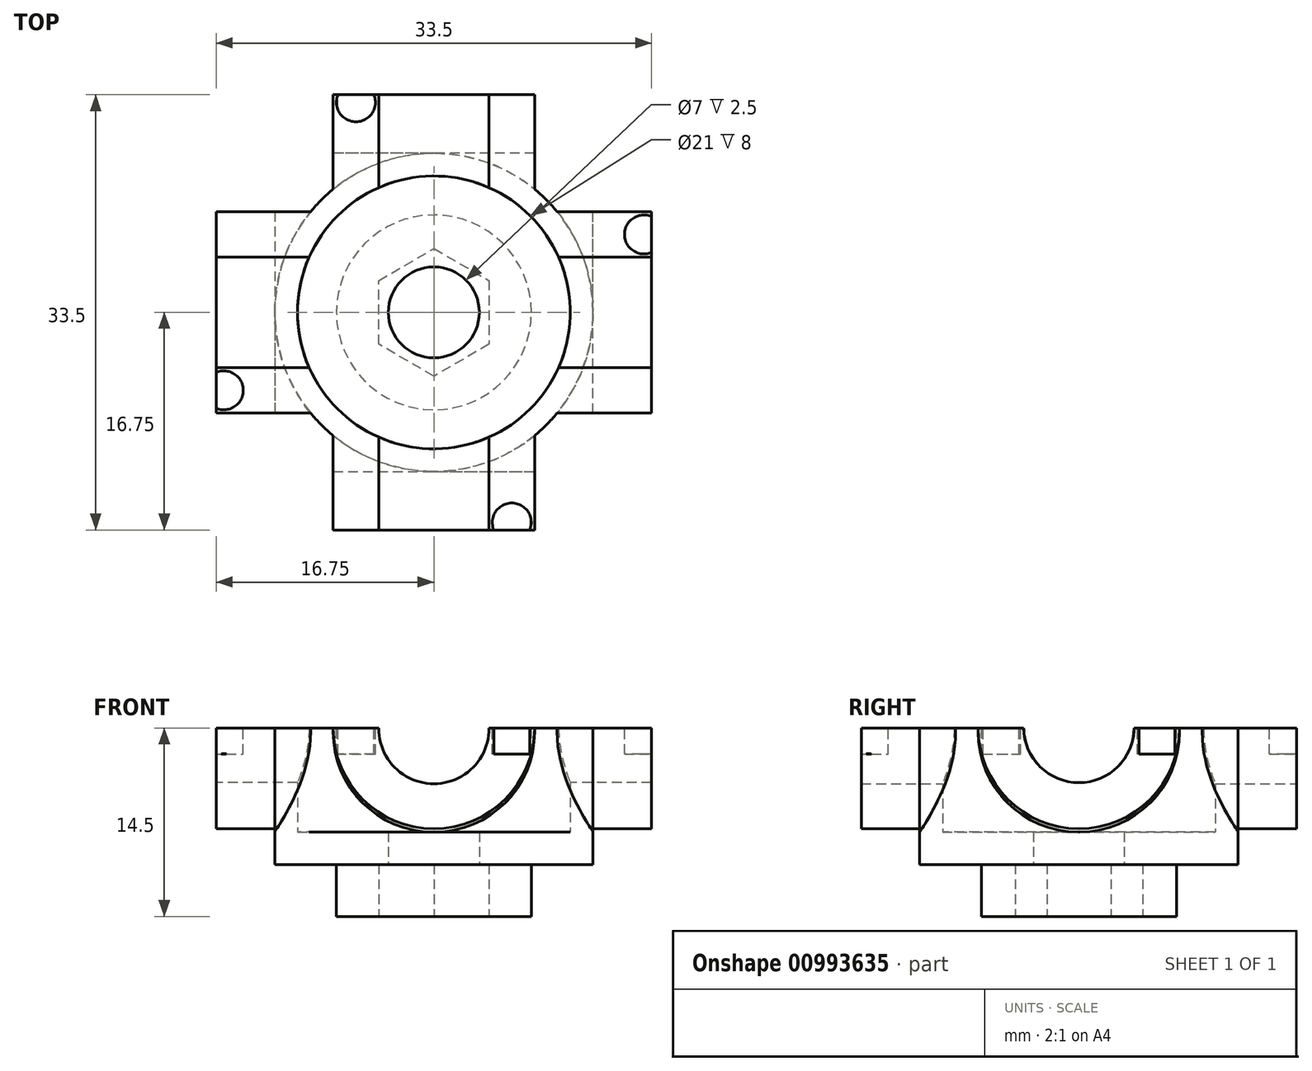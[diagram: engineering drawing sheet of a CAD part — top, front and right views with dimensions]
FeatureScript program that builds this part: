
annotation { "Feature Type Name" : "Feature", "Feature Type Description" : "" }
export const myFeature = defineFeature(function(context is Context, id is Id, definition is map)
    precondition{}
    {
        {
            var Q0;
            Q0=qCreatedBy(makeId("Top.planeOp"),FACE);
            var sketch = newSketch(context, id + "F0", { "sketchPlane" : qUnion([Q0])});
            skCircle(sketch, "E0.cCircle", {"center": v(0, 0) * mm, "radius": 4.25 * mm, "construction": true});
            skLineSegment(sketch, "E0.0", {"start": v(4.25, 2.45) * mm, "end": v(4.25, -2.45) * mm});
            skLineSegment(sketch, "E0.1", {"start": v(4.25, -2.45) * mm, "end": v(0, -4.9) * mm});
            skLineSegment(sketch, "E0.2", {"start": v(0, -4.9) * mm, "end": v(-4.25, -2.45) * mm});
            skLineSegment(sketch, "E0.3", {"start": v(-4.25, -2.45) * mm, "end": v(-4.25, 2.45) * mm});
            skLineSegment(sketch, "E0.4", {"start": v(-4.25, 2.45) * mm, "end": v(0, 4.9) * mm});
            skLineSegment(sketch, "E0.5", {"start": v(0, 4.9) * mm, "end": v(4.25, 2.45) * mm});
            skPoint(sketch, "E0.0.midPoint", {"position": v(4.25, 0) * mm});
            skCircle(sketch, "E1", {"center": v(0, 0) * mm, "radius": 3.5 * mm});
            skCircle(sketch, "E2", {"center": v(0, 0) * mm, "radius": 7.5 * mm});
            skSolve(sketch);
        }
        {
            var Q0;
            Q0=makeQuery(id+"F0.imprint","IMPRINT",FACE,{"disambiguationData":[TD([[makeQuery(id+"F0.imprint","IMPRINT",EDGE,{"derivedFrom":sQuery(id+"F0.wireOp",EDGE,"E0.0")}),1.0]])]});
            extrude(context, id + "F1", {"entities" : qUnion([Q0]), "depth" : 4 * mm, "offsetDistance" : 25 * mm});
        }
        {
            var Q0;
            Q0=makeQuery(id+"F1.opExtrude","CAP_FACE",FACE,{"disambiguationData":[OSD([sQuery(id+"F0.wireOp",EDGE,"E0.0"),sQuery(id+"F0.wireOp",EDGE,"E0.1"),sQuery(id+"F0.wireOp",EDGE,"E0.2"),sQuery(id+"F0.wireOp",EDGE,"E0.3"),sQuery(id+"F0.wireOp",EDGE,"E0.4"),sQuery(id+"F0.wireOp",EDGE,"E0.5"),sQuery(id+"F0.wireOp",EDGE,"E2")])],"isStart":false});
            var sketch = newSketch(context, id + "F2", { "sketchPlane" : qUnion([Q0])});
            skCircle(sketch, "E3", {"center": v(0, 0) * mm, "radius": 3.5 * mm});
            skCircle(sketch, "E4", {"center": v(0, 0) * mm, "radius": 12.25 * mm});
            skSolve(sketch);
        }
        {
            var Q0;
            Q0=makeQuery(id+"F2.imprint","IMPRINT",FACE,{"disambiguationData":[TD([[makeQuery(id+"F2.imprint","IMPRINT",EDGE,{"derivedFrom":sQuery(id+"F2.wireOp",EDGE,"E4")}),1.0]])]});
            var Q1;
            Q1=makeQuery(id+"F2.imprint","IMPRINT",FACE,{"disambiguationData":[TD([[makeQuery(id+"F2.imprint","IMPRINT",EDGE,{"derivedFrom":makeQuery(id+"F1.opExtrude","CAP_EDGE",EDGE,{"disambiguationData":[OSD([sQuery(id+"F0.wireOp",EDGE,"E0.0")])],"isStart":false})}),1.0]])]});
            var Q2;
            Q2=makeQuery(id+"F2.imprint","IMPRINT",FACE,{"disambiguationData":[TD([[makeQuery(id+"F2.imprint","IMPRINT",EDGE,{"derivedFrom":sQuery(id+"F2.wireOp",EDGE,"E3")}),-1.0]])]});
            extrude(context, id + "F3", {"entities" : qUnion([Q0, Q1, Q2]), "operationType" : NewBodyOperationType.ADD, "depth" : 2.5 * mm, "offsetDistance" : 25 * mm});
        }
        {
            var Q0;
            Q0=makeQuery(id+"F3.opExtrude","CAP_FACE",FACE,{"disambiguationData":[OSD([sQuery(id+"F2.wireOp",EDGE,"E3"),sQuery(id+"F2.wireOp",EDGE,"E4")])],"isStart":false});
            var sketch = newSketch(context, id + "F4", { "sketchPlane" : qUnion([Q0])});
            skLineSegment(sketch, "E5", {"start": v(0, 0) * mm, "end": v(-16.88, 16.88) * mm, "construction": true});
            skLineSegment(sketch, "E6", {"start": v(0, 0) * mm, "end": v(-26.34, 0) * mm, "construction": true});
            skCircle(sketch, "E7", {"center": v(0, 0) * mm, "radius": 16.75 * mm, "construction": true});
            skLineSegment(sketch, "E8", {"start": v(16.75, 0) * mm, "end": v(16.75, 7.75) * mm});
            skLineSegment(sketch, "E9", {"start": v(16.75, 7.75) * mm, "end": v(9.49, 7.75) * mm});
            skLineSegment(sketch, "E10", {"start": v(16.75, 0) * mm, "end": v(16.75, -7.75) * mm});
            skLineSegment(sketch, "E11", {"start": v(16.75, -7.75) * mm, "end": v(9.49, -7.75) * mm});
            skLineSegment(sketch, "E12.MirrorCS", {"start": v(-16.75, 7.75) * mm, "end": v(-9.49, 7.75) * mm});
            skLineSegment(sketch, "E13.MirrorCS", {"start": v(-16.75, 0) * mm, "end": v(-16.75, 7.75) * mm});
            skLineSegment(sketch, "E14.MirrorCS", {"start": v(-16.75, 0) * mm, "end": v(-16.75, -7.75) * mm});
            skLineSegment(sketch, "E15.MirrorCS", {"start": v(-16.75, -7.75) * mm, "end": v(-9.49, -7.75) * mm});
            skLineSegment(sketch, "E16.MirrorCS", {"start": v(-7.75, 16.75) * mm, "end": v(-7.75, 9.49) * mm});
            skLineSegment(sketch, "E17.MirrorCS", {"start": v(0, 16.75) * mm, "end": v(-7.75, 16.75) * mm});
            skLineSegment(sketch, "E18.MirrorCS", {"start": v(0, 16.75) * mm, "end": v(7.75, 16.75) * mm});
            skLineSegment(sketch, "E19.MirrorCS", {"start": v(7.75, 16.75) * mm, "end": v(7.75, 9.49) * mm});
            skLineSegment(sketch, "E20.MirrorCS", {"start": v(-7.75, -16.75) * mm, "end": v(-7.75, -9.49) * mm});
            skLineSegment(sketch, "E21.MirrorCS", {"start": v(0, -16.75) * mm, "end": v(-7.75, -16.75) * mm});
            skLineSegment(sketch, "E22.MirrorCS", {"start": v(0, -16.75) * mm, "end": v(7.75, -16.75) * mm});
            skLineSegment(sketch, "E23.MirrorCS", {"start": v(7.75, -16.75) * mm, "end": v(7.75, -9.49) * mm});
            skCircle(sketch, "E24", {"center": v(0, 0) * mm, "radius": 10.5 * mm});
            skSolve(sketch);
        }
        {
            var Q0;
            Q0=makeQuery(id+"F4.imprint","IMPRINT",FACE,{"disambiguationData":[TD([[makeQuery(id+"F4.imprint","IMPRINT",EDGE,{"derivedFrom":sQuery(id+"F4.wireOp",EDGE,"E24")}),-1.0]])]});
            var Q1;
            {var subQ1=sQuery(id+"F4.wireOp",EDGE,"E16.MirrorCS");Q1=makeQuery(id+"F4.imprint","IMPRINT",FACE,{"disambiguationData":[TD([[makeQuery(id+"F4.imprint","IMPRINT",EDGE,{"derivedFrom":subQ1}),1.0]])]});}
            var Q2;
            {var subQ1=sQuery(id+"F4.wireOp",EDGE,"E12.MirrorCS");Q2=makeQuery(id+"F4.imprint","IMPRINT",FACE,{"disambiguationData":[TD([[makeQuery(id+"F4.imprint","IMPRINT",EDGE,{"derivedFrom":subQ1}),-1.0]])]});}
            var Q3;
            Q3=makeQuery(id+"F4.imprint","IMPRINT",FACE,{"disambiguationData":[TD([[makeQuery(id+"F4.imprint","IMPRINT",EDGE,{"derivedFrom":sQuery(id+"F4.wireOp",EDGE,"E8")}),1.0]])]});
            var Q4;
            {var subQ1=sQuery(id+"F4.wireOp",EDGE,"E20.MirrorCS");Q4=makeQuery(id+"F4.imprint","IMPRINT",FACE,{"disambiguationData":[TD([[makeQuery(id+"F4.imprint","IMPRINT",EDGE,{"derivedFrom":subQ1}),-1.0]])]});}
            extrude(context, id + "F5", {"entities" : qUnion([Q0, Q1, Q2, Q3, Q4]), "operationType" : NewBodyOperationType.ADD, "depth" : 8 * mm, "offsetDistance" : 25 * mm});
        }
        {
            var Q0;
            Q0=makeQuery(id+"F5.opExtrude","SWEPT_FACE",FACE,{"disambiguationData":[OSD([sQuery(id+"F4.wireOp",EDGE,"E13.MirrorCS"),sQuery(id+"F4.wireOp",EDGE,"E14.MirrorCS")])]});
            var sketch = newSketch(context, id + "F6", { "sketchPlane" : qUnion([Q0])});
            skCircle(sketch, "E25", {"center": v(0, 14.5) * mm, "radius": 4.25 * mm, "construction": true});
            skArc(sketch, "E26", {"start": v(-4.25, 14.5) * mm, "mid": v(0, 10.3) * mm, "end": v(4.25, 14.5) * mm});
            skArc(sketch, "E27", {"start": v(-7.75, 14.5) * mm, "mid": v(0, 6.75) * mm, "end": v(7.75, 14.5) * mm});
            skSolve(sketch);
        }
        {
            var Q0;
            {var subQ0=sQuery(id+"F6.wireOp",EDGE,"E26");Q0=makeQuery(id+"F6.imprint","IMPRINT",FACE,{"disambiguationData":[TD([[makeQuery(id+"F6.imprint","IMPRINT",EDGE,{"derivedFrom":subQ0}),1.0]])]});}
            extrude(context, id + "F7", {"entities" : qUnion([Q0]), "operationType" : NewBodyOperationType.REMOVE, "endBound" : BoundingType.THROUGH_ALL, "oppositeDirection" : true, "depth" : 25 * mm, "offsetDistance" : 25 * mm});
        }
        {
            var Q0;
            Q0=makeQuery(id+"F6.imprint","IMPRINT",FACE,{"disambiguationData":[TD([[makeQuery(id+"F6.imprint","IMPRINT",EDGE,{"derivedFrom":sQuery(id+"F6.wireOp",EDGE,"E27")}),-1.0]])]});
            extrude(context, id + "F8", {"entities" : qUnion([Q0]), "operationType" : NewBodyOperationType.REMOVE, "oppositeDirection" : true, "depth" : 4.5 * mm, "offsetDistance" : 25 * mm});
        }
        {
            var Q0;
            Q0=makeQuery(id+"F5.opExtrude","SWEPT_FACE",FACE,{"disambiguationData":[OSD([sQuery(id+"F4.wireOp",EDGE,"E8"),sQuery(id+"F4.wireOp",EDGE,"E10")])]});
            var sketch = newSketch(context, id + "F9", { "sketchPlane" : qUnion([Q0])});
            skArc(sketch, "E28", {"start": v(-7.75, 14.5) * mm, "mid": v(0, 6.75) * mm, "end": v(7.75, 14.5) * mm});
            skSolve(sketch);
        }
        {
            var Q0;
            Q0=makeQuery(id+"F9.imprint","IMPRINT",FACE,{"disambiguationData":[TD([[makeQuery(id+"F9.imprint","IMPRINT",EDGE,{"derivedFrom":sQuery(id+"F9.wireOp",EDGE,"E28")}),-1.0]])]});
            extrude(context, id + "F10", {"entities" : qUnion([Q0]), "operationType" : NewBodyOperationType.REMOVE, "oppositeDirection" : true, "depth" : 4.5 * mm, "offsetDistance" : 25 * mm});
        }
        {
            var Q0;
            Q0=makeQuery(id+"F5.opExtrude","SWEPT_FACE",FACE,{"disambiguationData":[OSD([sQuery(id+"F4.wireOp",EDGE,"E17.MirrorCS"),sQuery(id+"F4.wireOp",EDGE,"E18.MirrorCS")])]});
            var sketch = newSketch(context, id + "F11", { "sketchPlane" : qUnion([Q0])});
            skCircle(sketch, "E29", {"center": v(0, 14.5) * mm, "radius": 4.25 * mm, "construction": true});
            skArc(sketch, "E30", {"start": v(-7.75, 14.5) * mm, "mid": v(0, 6.75) * mm, "end": v(7.75, 14.5) * mm});
            skArc(sketch, "E31", {"start": v(-4.25, 14.5) * mm, "mid": v(0, 10.21) * mm, "end": v(4.25, 14.5) * mm});
            skSolve(sketch);
        }
        {
            var Q0;
            {var subQ0=sQuery(id+"F11.wireOp",EDGE,"E31");Q0=makeQuery(id+"F11.imprint","IMPRINT",FACE,{"disambiguationData":[TD([[makeQuery(id+"F11.imprint","IMPRINT",EDGE,{"derivedFrom":subQ0}),1.0]])]});}
            extrude(context, id + "F12", {"entities" : qUnion([Q0]), "operationType" : NewBodyOperationType.REMOVE, "endBound" : BoundingType.THROUGH_ALL, "oppositeDirection" : true, "depth" : 25 * mm, "offsetDistance" : 25 * mm});
        }
        {
            var Q0;
            Q0=makeQuery(id+"F11.imprint","IMPRINT",FACE,{"disambiguationData":[TD([[makeQuery(id+"F11.imprint","IMPRINT",EDGE,{"derivedFrom":sQuery(id+"F11.wireOp",EDGE,"E30")}),-1.0]])]});
            extrude(context, id + "F13", {"entities" : qUnion([Q0]), "operationType" : NewBodyOperationType.REMOVE, "oppositeDirection" : true, "depth" : 4.5 * mm, "offsetDistance" : 25 * mm});
        }
        {
            var Q0;
            Q0=makeQuery(id+"F5.opExtrude","SWEPT_FACE",FACE,{"disambiguationData":[OSD([sQuery(id+"F4.wireOp",EDGE,"E21.MirrorCS"),sQuery(id+"F4.wireOp",EDGE,"E22.MirrorCS")])]});
            var sketch = newSketch(context, id + "F14", { "sketchPlane" : qUnion([Q0])});
            skArc(sketch, "E32", {"start": v(-7.75, 14.5) * mm, "mid": v(0, 6.75) * mm, "end": v(7.75, 14.5) * mm});
            skSolve(sketch);
        }
        {
            var Q0;
            Q0=makeQuery(id+"F14.imprint","IMPRINT",FACE,{"disambiguationData":[TD([[makeQuery(id+"F14.imprint","IMPRINT",EDGE,{"derivedFrom":sQuery(id+"F14.wireOp",EDGE,"E32")}),-1.0]])]});
            extrude(context, id + "F15", {"entities" : qUnion([Q0]), "operationType" : NewBodyOperationType.REMOVE, "oppositeDirection" : true, "depth" : 4.5 * mm, "offsetDistance" : 25 * mm});
        }
        {
            var Q0;
            Q0=makeQuery(id+"F5.opExtrude","CAP_EDGE",EDGE,{"disambiguationData":[OSD([sQuery(id+"F4.wireOp",EDGE,"E15.MirrorCS")])],"isStart":true});
            var Q1;
            Q1=makeQuery(id+"F5.opExtrude","CAP_EDGE",EDGE,{"disambiguationData":[OSD([sQuery(id+"F4.wireOp",EDGE,"E12.MirrorCS")])],"isStart":true});
            var Q2;
            Q2=makeQuery(id+"F5.opExtrude","CAP_EDGE",EDGE,{"disambiguationData":[OSD([sQuery(id+"F4.wireOp",EDGE,"E20.MirrorCS")])],"isStart":true});
            var Q3;
            Q3=makeQuery(id+"F5.opExtrude","CAP_EDGE",EDGE,{"disambiguationData":[OSD([sQuery(id+"F4.wireOp",EDGE,"E23.MirrorCS")])],"isStart":true});
            var Q4;
            Q4=makeQuery(id+"F5.opExtrude","CAP_EDGE",EDGE,{"disambiguationData":[OSD([sQuery(id+"F4.wireOp",EDGE,"E11")])],"isStart":true});
            var Q5;
            Q5=makeQuery(id+"F5.opExtrude","CAP_EDGE",EDGE,{"disambiguationData":[OSD([sQuery(id+"F4.wireOp",EDGE,"E9")])],"isStart":true});
            var Q6;
            Q6=makeQuery(id+"F5.opExtrude","CAP_EDGE",EDGE,{"disambiguationData":[OSD([sQuery(id+"F4.wireOp",EDGE,"E19.MirrorCS")])],"isStart":true});
            var Q7;
            Q7=makeQuery(id+"F5.opExtrude","CAP_EDGE",EDGE,{"disambiguationData":[OSD([sQuery(id+"F4.wireOp",EDGE,"E16.MirrorCS")])],"isStart":true});
            fillet(context, id + "F16", {"entities" : qUnion([Q0, Q1, Q2, Q3, Q4, Q5, Q6, Q7]), "radius" : 7.7 * mm, "tangentPropagation" : true, "allowEdgeOverflow" : false});
        }
        {
            var Q0;
            {var subQ0=sQuery(id+"F4.wireOp",EDGE,"E15.MirrorCS");var subQ1=sQuery(id+"F2.wireOp",EDGE,"E4");var subQ3=sQuery(id+"F4.wireOp",EDGE,"E20.MirrorCS");var subQ6=sQuery(id+"F4.wireOp",EDGE,"E14.MirrorCS");var subQ7=sQuery(id+"F4.wireOp",EDGE,"E13.MirrorCS");var subQ8=sQuery(id+"F4.wireOp",EDGE,"E12.MirrorCS");var subQ9=sQuery(id+"F4.wireOp",EDGE,"E9");var subQ10=sQuery(id+"F4.wireOp",EDGE,"E19.MirrorCS");var subQ12=sQuery(id+"F4.wireOp",EDGE,"E24");var subQ14=sQuery(id+"F4.wireOp",EDGE,"E18.MirrorCS");var subQ15=sQuery(id+"F4.wireOp",EDGE,"E17.MirrorCS");var subQ18=sQuery(id+"F4.wireOp",EDGE,"E11");var subQ19=sQuery(id+"F4.wireOp",EDGE,"E23.MirrorCS");var subQ21=makeQuery(id+"F5.opExtrude","SWEPT_FACE",FACE,{"disambiguationData":[OSD([subQ8])]});var subQ22=sQuery(id+"F4.wireOp",EDGE,"E16.MirrorCS");var subQ26=sQuery(id+"F4.wireOp",EDGE,"E10");var subQ27=sQuery(id+"F4.wireOp",EDGE,"E8");var subQ28=makeQuery(id+"F5.opExtrude","CAP_FACE",FACE,{"disambiguationData":[OSD([subQ1,subQ27,subQ9,subQ26,subQ18,subQ8,subQ7,subQ6,subQ0,subQ22,subQ15,subQ14,subQ10,subQ3,sQuery(id+"F4.wireOp",EDGE,"E21.MirrorCS"),sQuery(id+"F4.wireOp",EDGE,"E22.MirrorCS"),subQ19,subQ12])],"isStart":false});Q0=makeQuery(id+"F12.boolean.opBoolean","SPLIT",FACE,{"disambiguationData":[TD([subQ21])],"derivedFrom":makeQuery(id+"F7.boolean.opBoolean","SPLIT",FACE,{"disambiguationData":[TD([makeQuery(id+"F5.opExtrude","SWEPT_FACE",FACE,{"disambiguationData":[OSD([subQ9])]})])],"derivedFrom":subQ28})});}
            var sketch = newSketch(context, id + "F17", { "sketchPlane" : qUnion([Q0])});
            skLineSegment(sketch, "E33", {"start": v(0, 0) * mm, "end": v(16.6, 16.6) * mm, "construction": true});
            skLineSegment(sketch, "E34", {"start": v(0, 0) * mm, "end": v(22.28, 0) * mm, "construction": true});
            skCircle(sketch, "E35", {"center": v(0, 0) * mm, "radius": 17.25 * mm, "construction": true});
            skCircle(sketch, "E36", {"center": v(0, 0) * mm, "radius": 6 * mm, "construction": true});
            skLineSegment(sketch, "E37", {"start": v(-6, 0) * mm, "end": v(-6, 19.71) * mm, "construction": true});
            skLineSegment(sketch, "E38", {"start": v(6, 0) * mm, "end": v(6, 19.18) * mm, "construction": true});
            skLineSegment(sketch, "E39", {"start": v(0, 6) * mm, "end": v(19.02, 6) * mm, "construction": true});
            skLineSegment(sketch, "E40", {"start": v(0, -6) * mm, "end": v(19.02, -6) * mm, "construction": true});
            skCircle(sketch, "E41", {"center": v(-6, 16.17) * mm, "radius": 1.5 * mm});
            skCircle(sketch, "E42.MirrorC", {"center": v(6, 16.17) * mm, "radius": 1.5 * mm});
            skCircle(sketch, "E43.MirrorC", {"center": v(6, -16.17) * mm, "radius": 1.5 * mm});
            skCircle(sketch, "E44.MirrorC", {"center": v(-6, -16.17) * mm, "radius": 1.5 * mm});
            skCircle(sketch, "E45.MirrorC", {"center": v(16.17, 6) * mm, "radius": 1.5 * mm});
            skCircle(sketch, "E46.MirrorC", {"center": v(16.17, -6) * mm, "radius": 1.5 * mm});
            skCircle(sketch, "E47.MirrorC", {"center": v(-16.17, 6) * mm, "radius": 1.5 * mm});
            skCircle(sketch, "E48.MirrorC", {"center": v(-16.17, -6) * mm, "radius": 1.5 * mm});
            skSolve(sketch);
        }
        {
            var Q0;
            {var subQ0=sQuery(id+"F17.wireOp",EDGE,"E41");var subQ1=sQuery(id+"F4.wireOp",EDGE,"E18.MirrorCS");var subQ2=sQuery(id+"F4.wireOp",EDGE,"E17.MirrorCS");var subQ3=sQuery(id+"F4.wireOp",EDGE,"E16.MirrorCS");var subQ4=makeQuery(id+"F12.boolean.opBoolean","SPLIT",EDGE,{"disambiguationData":[TD([makeQuery(id+"F5.opExtrude","SWEPT_FACE",FACE,{"disambiguationData":[OSD([subQ3])]})])],"derivedFrom":makeQuery(id+"F5.opExtrude","CAP_EDGE",EDGE,{"disambiguationData":[OSD([subQ2,subQ1])],"isStart":false})});var subQ5=makeQuery(id+"F17.imprint","INTERSECT",VERTEX,{"disambiguationData":[OD(0.0)],"derivedFrom":[subQ4,subQ0]});Q0=makeQuery(id+"F17.imprint","IMPRINT",FACE,{"disambiguationData":[TD([[makeQuery(id+"F17.imprint","IMPRINT",EDGE,{"disambiguationData":[TD([[subQ5,1.0]])],"derivedFrom":subQ0}),1.0]])]});}
            var Q1;
            Q1=makeQuery(id+"F17.imprint","IMPRINT",FACE,{"disambiguationData":[TD([[makeQuery(id+"F17.imprint","IMPRINT",EDGE,{"derivedFrom":sQuery(id+"F17.wireOp",EDGE,"E42.MirrorC")}),-1.0]])]});
            var Q2;
            Q2=makeQuery(id+"F17.imprint","IMPRINT",FACE,{"disambiguationData":[TD([[makeQuery(id+"F17.imprint","IMPRINT",EDGE,{"derivedFrom":sQuery(id+"F17.wireOp",EDGE,"E46.MirrorC")}),-1.0]])]});
            var Q3;
            Q3=makeQuery(id+"F17.imprint","IMPRINT",FACE,{"disambiguationData":[TD([[makeQuery(id+"F17.imprint","IMPRINT",EDGE,{"derivedFrom":sQuery(id+"F17.wireOp",EDGE,"E45.MirrorC")}),1.0]])]});
            var Q4;
            Q4=makeQuery(id+"F17.imprint","IMPRINT",FACE,{"disambiguationData":[TD([[makeQuery(id+"F17.imprint","IMPRINT",EDGE,{"derivedFrom":sQuery(id+"F17.wireOp",EDGE,"E44.MirrorC")}),-1.0]])]});
            var Q5;
            Q5=makeQuery(id+"F17.imprint","IMPRINT",FACE,{"disambiguationData":[TD([[makeQuery(id+"F17.imprint","IMPRINT",EDGE,{"derivedFrom":sQuery(id+"F17.wireOp",EDGE,"E43.MirrorC")}),1.0]])]});
            var Q6;
            {var subQ0=sQuery(id+"F17.wireOp",EDGE,"E47.MirrorC");var subQ1=sQuery(id+"F4.wireOp",EDGE,"E14.MirrorCS");var subQ2=sQuery(id+"F4.wireOp",EDGE,"E13.MirrorCS");var subQ3=sQuery(id+"F4.wireOp",EDGE,"E12.MirrorCS");var subQ4=makeQuery(id+"F7.boolean.opBoolean","SPLIT",EDGE,{"disambiguationData":[TD([makeQuery(id+"F5.opExtrude","SWEPT_FACE",FACE,{"disambiguationData":[OSD([subQ3])]})])],"derivedFrom":makeQuery(id+"F5.opExtrude","CAP_EDGE",EDGE,{"disambiguationData":[OSD([subQ2,subQ1])],"isStart":false})});var subQ5=makeQuery(id+"F17.imprint","INTERSECT",VERTEX,{"disambiguationData":[OD(0.0)],"derivedFrom":[subQ4,subQ0]});Q6=makeQuery(id+"F17.imprint","IMPRINT",FACE,{"disambiguationData":[TD([[makeQuery(id+"F17.imprint","IMPRINT",EDGE,{"disambiguationData":[TD([[subQ5,1.0]])],"derivedFrom":subQ0}),-1.0]])]});}
            var Q7;
            Q7=makeQuery(id+"F17.imprint","IMPRINT",FACE,{"disambiguationData":[TD([[makeQuery(id+"F17.imprint","IMPRINT",EDGE,{"derivedFrom":sQuery(id+"F17.wireOp",EDGE,"E48.MirrorC")}),1.0]])]});
            extrude(context, id + "F18", {"entities" : qUnion([Q0, Q1, Q2, Q3, Q4, Q5, Q6, Q7]), "operationType" : NewBodyOperationType.REMOVE, "oppositeDirection" : true, "depth" : 2 * mm, "offsetDistance" : 25 * mm});
        }
    });
